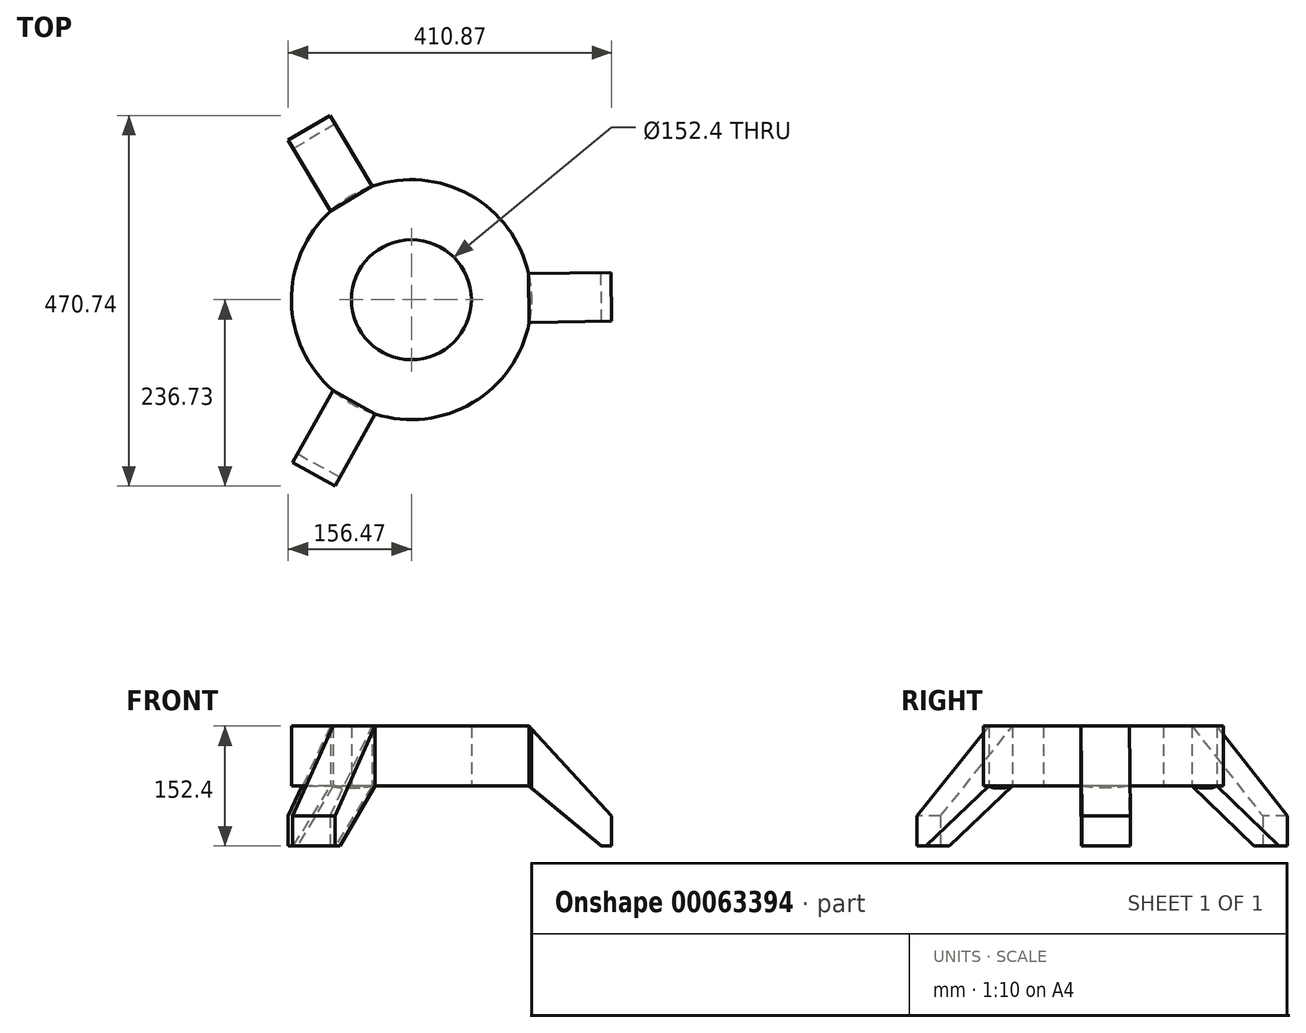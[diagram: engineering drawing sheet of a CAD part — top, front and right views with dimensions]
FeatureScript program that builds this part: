
annotation { "Feature Type Name" : "Feature", "Feature Type Description" : "" }
export const myFeature = defineFeature(function(context is Context, id is Id, definition is map)
    precondition{}
    {
        {
            var Q0;
            Q0=qCreatedBy(makeId("Top.planeOp"),FACE);
            var sketch = newSketch(context, id + "F0", { "sketchPlane" : qUnion([Q0])});
            skCircle(sketch, "E0", {"center": v(0, 0) * mm, "radius": 76.2 * mm});
            skCircle(sketch, "E1", {"center": v(0, 0) * mm, "radius": 152.4 * mm});
            skCircle(sketch, "E2.cCircle", {"center": v(0, 0) * mm, "radius": 152.4 * mm, "construction": true});
            skLineSegment(sketch, "E3", {"start": v(-101.32, -117.95) * mm, "end": v(-150.92, -206.62) * mm});
            skLineSegment(sketch, "E4", {"start": v(-150.92, -206.62) * mm, "end": v(-97.09, -236.73) * mm});
            skLineSegment(sketch, "E5", {"start": v(-97.09, -236.73) * mm, "end": v(-47.49, -148.06) * mm});
            skLineSegment(sketch, "E6", {"start": v(152.8, -28.77) * mm, "end": v(254.4, -27.39) * mm});
            skLineSegment(sketch, "E7", {"start": v(254.4, -27.39) * mm, "end": v(253.56, 34.28) * mm});
            skLineSegment(sketch, "E8", {"start": v(253.56, 34.28) * mm, "end": v(151.97, 32.9) * mm});
            skLineSegment(sketch, "E9", {"start": v(-104.48, 115.16) * mm, "end": v(-156.47, 202.45) * mm});
            skLineSegment(sketch, "E10", {"start": v(-156.47, 202.45) * mm, "end": v(-103.48, 234) * mm});
            skLineSegment(sketch, "E11", {"start": v(-103.48, 234) * mm, "end": v(-51.49, 146.72) * mm});
            skLineSegment(sketch, "E12", {"start": v(151.97, 32.9) * mm, "end": v(148.82, 32.86) * mm});
            skLineSegment(sketch, "E13", {"start": v(152.8, -28.77) * mm, "end": v(149.66, -28.77) * mm});
            skLineSegment(sketch, "E14", {"start": v(-104.48, 115.16) * mm, "end": v(-102.87, 112.45) * mm});
            skLineSegment(sketch, "E15", {"start": v(-51.49, 146.72) * mm, "end": v(-49.88, 144) * mm});
            skLineSegment(sketch, "E16", {"start": v(-101.32, -117.95) * mm, "end": v(-99.78, -115.2) * mm});
            skLineSegment(sketch, "E17", {"start": v(-47.49, -148.06) * mm, "end": v(-45.95, -145.3) * mm});
            skSolve(sketch);
        }
        {
            var Q0;
            Q0=makeQuery(id+"F0.imprint","IMPRINT",FACE,{"disambiguationData":[TD([[makeQuery(id+"F0.imprint","IMPRINT",EDGE,{"derivedFrom":sQuery(id+"F0.wireOp",EDGE,"E9")}),-1.0]])]});
            var Q1;
            Q1=makeQuery(id+"F0.imprint","IMPRINT",FACE,{"disambiguationData":[TD([[makeQuery(id+"F0.imprint","IMPRINT",EDGE,{"derivedFrom":sQuery(id+"F0.wireOp",EDGE,"E0")}),-1.0]])]});
            var Q2;
            Q2=makeQuery(id+"F0.imprint","IMPRINT",FACE,{"disambiguationData":[TD([[makeQuery(id+"F0.imprint","IMPRINT",EDGE,{"derivedFrom":sQuery(id+"F0.wireOp",EDGE,"E3")}),1.0]])]});
            var Q3;
            Q3=makeQuery(id+"F0.imprint","IMPRINT",FACE,{"disambiguationData":[TD([[makeQuery(id+"F0.imprint","IMPRINT",EDGE,{"derivedFrom":sQuery(id+"F0.wireOp",EDGE,"E6")}),1.0]])]});
            extrude(context, id + "F1", {"entities" : qUnion([Q0, Q1, Q2, Q3]), "depth" : 152.4 * mm});
        }
        {
            var Q0;
            Q0=makeQuery(id+"F1.opExtrude","CAP_FACE",FACE,{"disambiguationData":[OSD([sQuery(id+"F0.wireOp",EDGE,"E0"),sQuery(id+"F0.wireOp",EDGE,"E1"),sQuery(id+"F0.wireOp",EDGE,"E3"),sQuery(id+"F0.wireOp",EDGE,"E4"),sQuery(id+"F0.wireOp",EDGE,"E5"),sQuery(id+"F0.wireOp",EDGE,"E6"),sQuery(id+"F0.wireOp",EDGE,"E7"),sQuery(id+"F0.wireOp",EDGE,"E8"),sQuery(id+"F0.wireOp",EDGE,"E9"),sQuery(id+"F0.wireOp",EDGE,"E10"),sQuery(id+"F0.wireOp",EDGE,"E11"),sQuery(id+"F0.wireOp",EDGE,"E12"),sQuery(id+"F0.wireOp",EDGE,"E13"),sQuery(id+"F0.wireOp",EDGE,"E14"),sQuery(id+"F0.wireOp",EDGE,"E15"),sQuery(id+"F0.wireOp",EDGE,"E16"),sQuery(id+"F0.wireOp",EDGE,"E17")])],"isStart":true});
            var sketch = newSketch(context, id + "F2", { "sketchPlane" : qUnion([Q0])});
            skCircle(sketch, "E18", {"center": v(0, 0) * mm, "radius": 76.2 * mm});
            skCircle(sketch, "E19", {"center": v(0, 0) * mm, "radius": 152.4 * mm});
            skSolve(sketch);
        }
        {
            var Q0;
            Q0=makeQuery(id+"F2.imprint","IMPRINT",FACE,{"disambiguationData":[TD([[makeQuery(id+"F2.imprint","IMPRINT",EDGE,{"derivedFrom":sQuery(id+"F2.wireOp",EDGE,"E18")}),1.0]])]});
            extrude(context, id + "F3", {"entities" : qUnion([Q0]), "operationType" : NewBodyOperationType.REMOVE, "oppositeDirection" : true, "depth" : 76.2 * mm});
        }
        {
            var Q0;
            Q0=makeQuery(id+"F1.opExtrude","SWEPT_FACE",FACE,{"disambiguationData":[OSD([sQuery(id+"F0.wireOp",EDGE,"E8"),sQuery(id+"F0.wireOp",EDGE,"E12")])]});
            var sketch = newSketch(context, id + "F4", { "sketchPlane" : qUnion([Q0])});
            skLineSegment(sketch, "E20", {"start": v(-149.25, 152.4) * mm, "end": v(-254, 38.1) * mm});
            skLineSegment(sketch, "E21", {"start": v(-254, 38.1) * mm, "end": v(-254, 0) * mm});
            skLineSegment(sketch, "E22", {"start": v(-254, 0) * mm, "end": v(-241.3, 0) * mm});
            skLineSegment(sketch, "E23", {"start": v(-241.3, 0) * mm, "end": v(-149.25, 76.2) * mm});
            skLineSegment(sketch, "E24", {"start": v(-149.25, 76.2) * mm, "end": v(-149.25, 152.4) * mm});
            skSolve(sketch);
        }
        {
            var Q0;
            {var subQ0=sQuery(id+"F4.wireOp",EDGE,"E20");Q0=makeQuery(id+"F4.imprint","IMPRINT",FACE,{"disambiguationData":[TD([[makeQuery(id+"F4.imprint","IMPRINT",EDGE,{"derivedFrom":subQ0}),-1.0]])]});}
            var Q1;
            {var subQ0=sQuery(id+"F4.wireOp",EDGE,"E23");Q1=makeQuery(id+"F4.imprint","IMPRINT",FACE,{"disambiguationData":[TD([[makeQuery(id+"F4.imprint","IMPRINT",EDGE,{"derivedFrom":subQ0}),-1.0]])]});}
            extrude(context, id + "F5", {"entities" : qUnion([Q0, Q1]), "operationType" : NewBodyOperationType.REMOVE, "oppositeDirection" : true, "depth" : 76.2 * mm});
        }
        {
            var Q0;
            Q0=makeQuery(id+"F1.opExtrude","SWEPT_FACE",FACE,{"disambiguationData":[OSD([sQuery(id+"F0.wireOp",EDGE,"E9"),sQuery(id+"F0.wireOp",EDGE,"E14")])]});
            var sketch = newSketch(context, id + "F6", { "sketchPlane" : qUnion([Q0])});
            skLineSegment(sketch, "E25", {"start": v(-149.25, 152.4) * mm, "end": v(-254, 38.1) * mm});
            skLineSegment(sketch, "E26", {"start": v(-254, 38.1) * mm, "end": v(-254, 0) * mm});
            skLineSegment(sketch, "E27", {"start": v(-254, 0) * mm, "end": v(-241.3, 0) * mm});
            skLineSegment(sketch, "E28", {"start": v(-241.3, 0) * mm, "end": v(-149.25, 76.2) * mm});
            skLineSegment(sketch, "E29", {"start": v(-149.25, 76.2) * mm, "end": v(-149.25, 152.4) * mm});
            skSolve(sketch);
        }
        {
            var Q0;
            {var subQ0=sQuery(id+"F6.wireOp",EDGE,"E25");Q0=makeQuery(id+"F6.imprint","IMPRINT",FACE,{"disambiguationData":[TD([[makeQuery(id+"F6.imprint","IMPRINT",EDGE,{"derivedFrom":subQ0}),-1.0]])]});}
            var Q1;
            {var subQ0=sQuery(id+"F6.wireOp",EDGE,"E28");Q1=makeQuery(id+"F6.imprint","IMPRINT",FACE,{"disambiguationData":[TD([[makeQuery(id+"F6.imprint","IMPRINT",EDGE,{"derivedFrom":subQ0}),-1.0]])]});}
            extrude(context, id + "F7", {"entities" : qUnion([Q0, Q1]), "operationType" : NewBodyOperationType.REMOVE, "oppositeDirection" : true, "depth" : 76.2 * mm});
        }
        {
            var Q0;
            Q0=makeQuery(id+"F1.opExtrude","SWEPT_FACE",FACE,{"disambiguationData":[OSD([sQuery(id+"F0.wireOp",EDGE,"E5"),sQuery(id+"F0.wireOp",EDGE,"E17")])]});
            var sketch = newSketch(context, id + "F8", { "sketchPlane" : qUnion([Q0])});
            skLineSegment(sketch, "E30", {"start": v(-149.25, 152.4) * mm, "end": v(-254, 38.1) * mm});
            skLineSegment(sketch, "E31", {"start": v(-254, 38.1) * mm, "end": v(-254, 0) * mm});
            skLineSegment(sketch, "E32", {"start": v(-254, 0) * mm, "end": v(-241.3, 0) * mm});
            skLineSegment(sketch, "E33", {"start": v(-241.3, 0) * mm, "end": v(-149.25, 76.2) * mm});
            skLineSegment(sketch, "E34", {"start": v(-149.25, 76.2) * mm, "end": v(-149.25, 152.4) * mm});
            skSolve(sketch);
        }
        {
            var Q0;
            {var subQ0=sQuery(id+"F8.wireOp",EDGE,"E30");Q0=makeQuery(id+"F8.imprint","IMPRINT",FACE,{"disambiguationData":[TD([[makeQuery(id+"F8.imprint","IMPRINT",EDGE,{"derivedFrom":subQ0}),-1.0]])]});}
            var Q1;
            {var subQ0=sQuery(id+"F8.wireOp",EDGE,"E33");Q1=makeQuery(id+"F8.imprint","IMPRINT",FACE,{"disambiguationData":[TD([[makeQuery(id+"F8.imprint","IMPRINT",EDGE,{"derivedFrom":subQ0}),-1.0]])]});}
            extrude(context, id + "F9", {"entities" : qUnion([Q0, Q1]), "operationType" : NewBodyOperationType.REMOVE, "oppositeDirection" : true, "depth" : 76.2 * mm});
        }
    });
